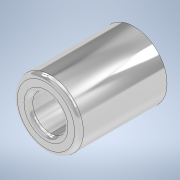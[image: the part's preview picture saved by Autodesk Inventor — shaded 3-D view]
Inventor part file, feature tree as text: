
AUTODESK INVENTOR PART (.ipt)
format: ipt  version: 2021 (Build 250183000, 183)  size: 129,024 bytes
history: native  units: mm
features: other x1, extrude x1, fillet x1, sketch x1
ambient origin geometry x8: Origin, YZ Plane, XZ Plane, XY Plane, X Axis, Y Axis, Z Axis, Center Point
bodies: Body1 (feature_tree)
feature tree (4):
  other  "Sólido1"
  extrude  "Extrusão1"  Depth=2.0mm
  fillet  "Arredondamento1"  Radius=40.0mm
  sketch  "Esboço1"  dims[d0=30.0mm d1=16.0mm d2=40.0mm d3=0.0mm d4=2.0mm]
